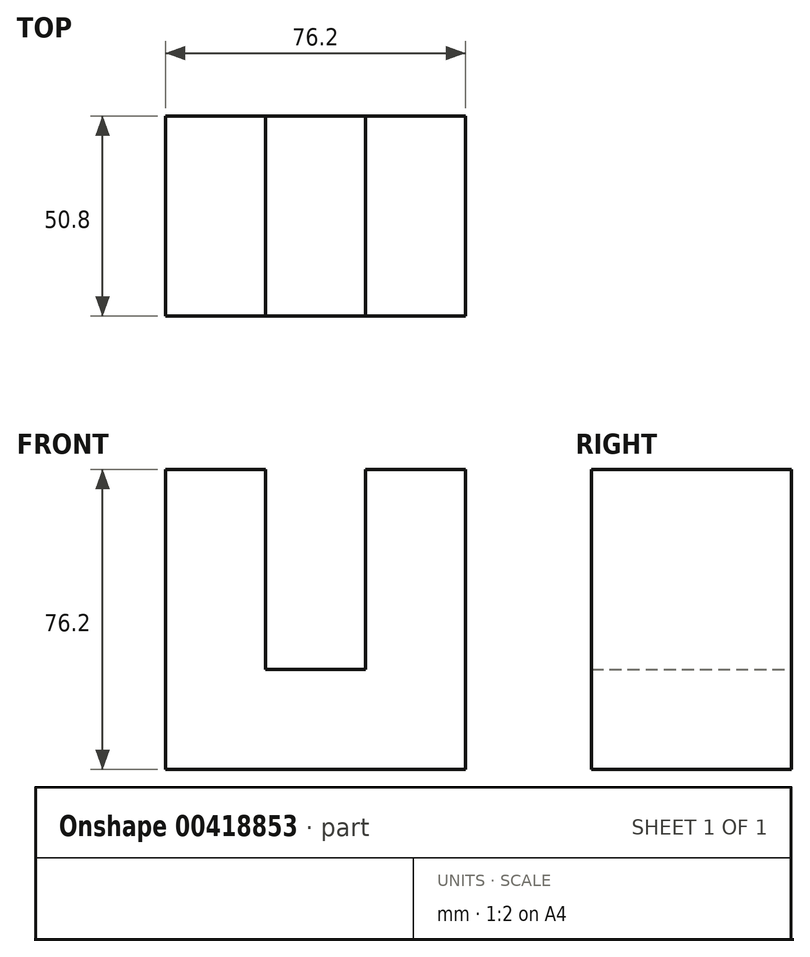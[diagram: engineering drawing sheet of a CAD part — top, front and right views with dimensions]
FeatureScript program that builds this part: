
annotation { "Feature Type Name" : "Feature", "Feature Type Description" : "" }
export const myFeature = defineFeature(function(context is Context, id is Id, definition is map)
    precondition{}
    {
        {
            var Q0;
            Q0=qCreatedBy(makeId("Front.planeOp"),FACE);
            var sketch = newSketch(context, id + "F0", { "sketchPlane" : qUnion([Q0])});
            skLineSegment(sketch, "E0", {"start": v(0, 0) * mm, "end": v(-76.2, 0) * mm});
            skLineSegment(sketch, "E1", {"start": v(-76.2, 0) * mm, "end": v(-76.2, 76.2) * mm});
            skLineSegment(sketch, "E2", {"start": v(-76.2, 76.2) * mm, "end": v(-50.8, 76.2) * mm});
            skLineSegment(sketch, "E3", {"start": v(-50.8, 76.2) * mm, "end": v(-50.8, 25.4) * mm});
            skLineSegment(sketch, "E4", {"start": v(0, 0) * mm, "end": v(0, 76.2) * mm});
            skLineSegment(sketch, "E5", {"start": v(0, 76.2) * mm, "end": v(-25.4, 76.2) * mm});
            skLineSegment(sketch, "E6", {"start": v(-25.4, 76.2) * mm, "end": v(-25.4, 25.4) * mm});
            skLineSegment(sketch, "E7", {"start": v(-50.8, 25.4) * mm, "end": v(-25.4, 25.4) * mm});
            skSolve(sketch);
        }
        {
            var Q0;
            Q0 = qSketchRegion(id + "F0", true);
            extrude(context, id + "F1", {"entities" : qUnion([Q0]), "depth" : 50.8 * mm});
        }
    });
